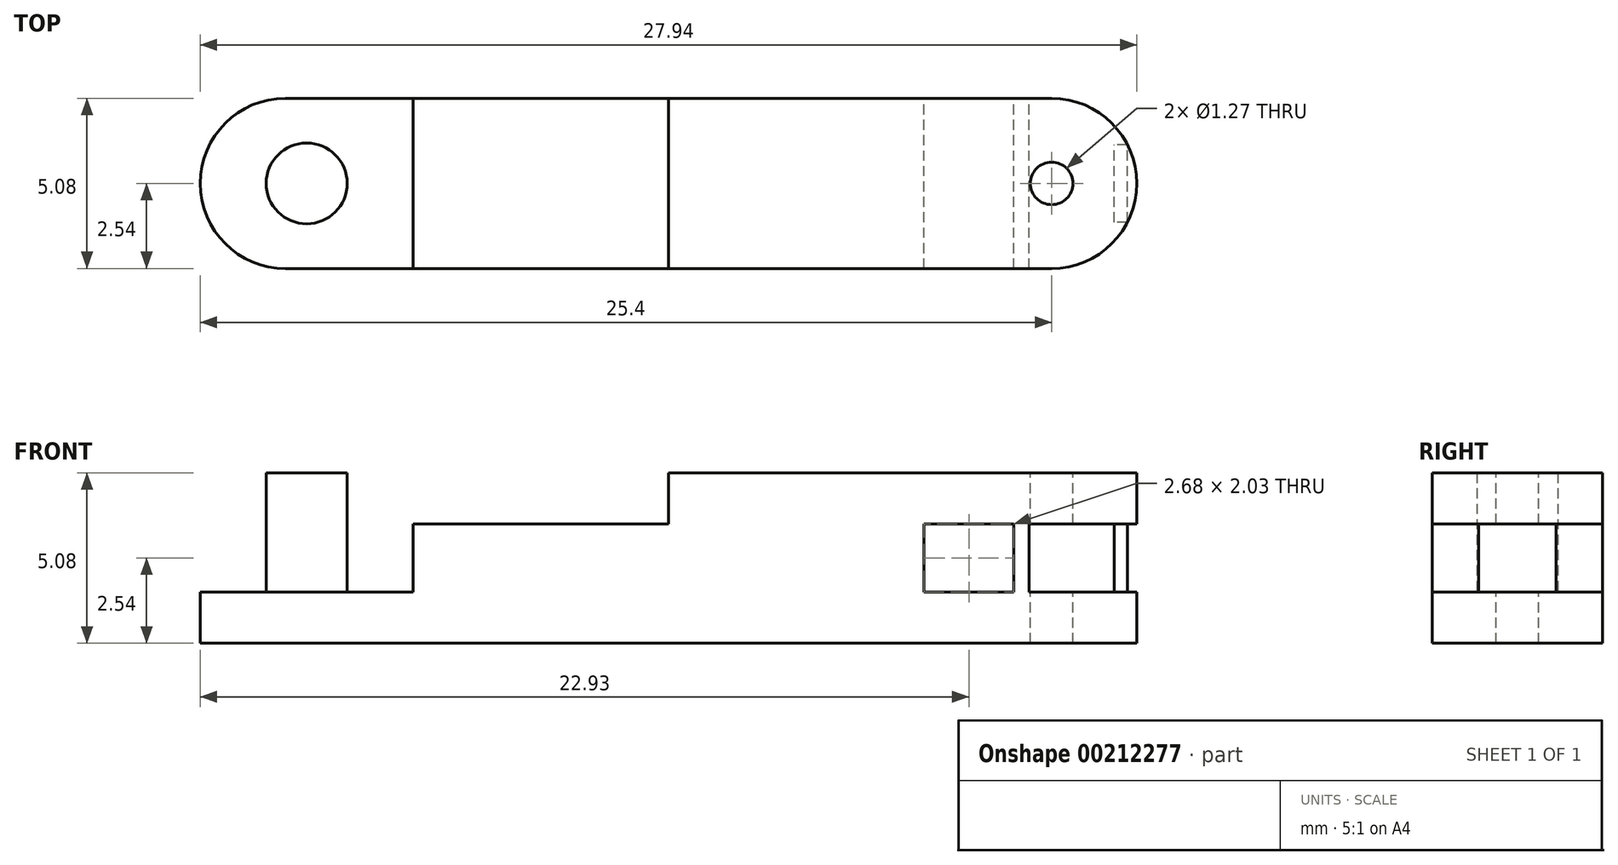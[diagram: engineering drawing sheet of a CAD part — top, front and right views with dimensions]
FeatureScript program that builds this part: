
annotation { "Feature Type Name" : "Feature", "Feature Type Description" : "" }
export const myFeature = defineFeature(function(context is Context, id is Id, definition is map)
    precondition{}
    {
        {
            var Q0;
            Q0=qCreatedBy(makeId("Top.planeOp"),FACE);
            var sketch = newSketch(context, id + "F0", { "sketchPlane" : qUnion([Q0])});
            skLineSegment(sketch, "E0.bottom", {"start": v(13.97, -2.54) * mm, "end": v(-13.97, -2.54) * mm});
            skLineSegment(sketch, "E0.top", {"start": v(13.97, 2.54) * mm, "end": v(-13.97, 2.54) * mm});
            skLineSegment(sketch, "E0.left", {"start": v(13.97, -2.54) * mm, "end": v(13.97, 2.54) * mm});
            skLineSegment(sketch, "E0.right", {"start": v(-13.97, -2.54) * mm, "end": v(-13.97, 2.54) * mm});
            skPoint(sketch, "E0.middle", {"position": v(0, 0) * mm});
            skSolve(sketch);
        }
        {
            var Q0;
            Q0=makeQuery(id+"F0.imprint","IMPRINT",FACE,{"disambiguationData":[TD([[makeQuery(id+"F0.imprint","IMPRINT",EDGE,{"derivedFrom":sQuery(id+"F0.wireOp",EDGE,"E0.bottom")}),-1.0]])]});
            extrude(context, id + "F1", {"entities" : qUnion([Q0]), "depth" : 1.52 * mm});
        }
        {
            var Q0;
            Q0=makeQuery(id+"F1.opExtrude","CAP_FACE",FACE,{"disambiguationData":[OSD([sQuery(id+"F0.wireOp",EDGE,"E0.bottom"),sQuery(id+"F0.wireOp",EDGE,"E0.top"),sQuery(id+"F0.wireOp",EDGE,"E0.left"),sQuery(id+"F0.wireOp",EDGE,"E0.right")])],"isStart":false});
            var sketch = newSketch(context, id + "F2", { "sketchPlane" : qUnion([Q0])});
            skLineSegment(sketch, "E1.bottom", {"start": v(7.62, -2.54) * mm, "end": v(-7.62, -2.54) * mm});
            skLineSegment(sketch, "E1.top", {"start": v(7.62, 2.54) * mm, "end": v(-7.62, 2.54) * mm});
            skLineSegment(sketch, "E1.left", {"start": v(7.62, -2.54) * mm, "end": v(7.62, 2.54) * mm});
            skLineSegment(sketch, "E1.right", {"start": v(-7.62, -2.54) * mm, "end": v(-7.62, 2.54) * mm});
            skPoint(sketch, "E1.middle", {"position": v(0, 0) * mm});
            skSolve(sketch);
        }
        {
            var Q0;
            Q0=makeQuery(id+"F2.imprint","IMPRINT",FACE,{"disambiguationData":[TD([[makeQuery(id+"F2.imprint","IMPRINT",EDGE,{"derivedFrom":sQuery(id+"F2.wireOp",EDGE,"E1.bottom")}),-1.0]])]});
            extrude(context, id + "F3", {"entities" : qUnion([Q0]), "operationType" : NewBodyOperationType.ADD, "depth" : 2.03 * mm});
        }
        {
            var Q0;
            {var subQ0=sQuery(id+"F0.wireOp",EDGE,"E0.right");var subQ1=sQuery(id+"F0.wireOp",EDGE,"E0.top");var subQ2=sQuery(id+"F0.wireOp",EDGE,"E0.bottom");Q0=makeQuery(id+"F3.boolean.opBoolean","SPLIT",FACE,{"disambiguationData":[TD([makeQuery(id+"F1.opExtrude","SWEPT_FACE",FACE,{"disambiguationData":[OSD([subQ0])]})])],"derivedFrom":makeQuery(id+"F1.opExtrude","CAP_FACE",FACE,{"disambiguationData":[OSD([subQ2,subQ1,sQuery(id+"F0.wireOp",EDGE,"E0.left"),subQ0])],"isStart":false})});}
            var sketch = newSketch(context, id + "F4", { "sketchPlane" : qUnion([Q0])});
            skCircle(sketch, "E2", {"center": v(-10.8, 0) * mm, "radius": 1.2 * mm});
            skSolve(sketch);
        }
        {
            var Q0;
            Q0=makeQuery(id+"F4.imprint","IMPRINT",FACE,{"disambiguationData":[TD([[makeQuery(id+"F4.imprint","IMPRINT",EDGE,{"derivedFrom":sQuery(id+"F4.wireOp",EDGE,"E2")}),1.0]])]});
            var Q1;
            Q1=sQuery(id+"F4.wireOp",EDGE,"E2");
            extrude(context, id + "F5", {"entities" : qUnion([Q0]), "operationType" : NewBodyOperationType.ADD, "surfaceEntities" : qUnion([Q1]), "depth" : 3.56 * mm});
        }
        {
            var Q0;
            Q0=makeQuery(id+"F3.opExtrude","CAP_FACE",FACE,{"disambiguationData":[OSD([sQuery(id+"F2.wireOp",EDGE,"E1.bottom"),sQuery(id+"F2.wireOp",EDGE,"E1.top"),sQuery(id+"F2.wireOp",EDGE,"E1.left"),sQuery(id+"F2.wireOp",EDGE,"E1.right")])],"isStart":false});
            var sketch = newSketch(context, id + "F6", { "sketchPlane" : qUnion([Q0])});
            skLineSegment(sketch, "E3.bottom", {"start": v(0, -2.54) * mm, "end": v(13.97, -2.54) * mm});
            skLineSegment(sketch, "E3.top", {"start": v(0, 2.54) * mm, "end": v(13.97, 2.54) * mm});
            skLineSegment(sketch, "E3.left", {"start": v(0, -2.54) * mm, "end": v(0, 2.54) * mm});
            skLineSegment(sketch, "E3.right", {"start": v(13.97, -2.54) * mm, "end": v(13.97, 2.54) * mm});
            skSolve(sketch);
        }
        {
            var Q0;
            Q0 = qSketchRegion(id + "F6", true);
            extrude(context, id + "F7", {"entities" : qUnion([Q0]), "operationType" : NewBodyOperationType.ADD, "depth" : 1.52 * mm});
        }
        {
            var Q0;
            Q0=makeQuery(id+"F7.opExtrude","CAP_FACE",FACE,{"disambiguationData":[OSD([sQuery(id+"F6.wireOp",EDGE,"E3.bottom"),sQuery(id+"F6.wireOp",EDGE,"E3.top"),sQuery(id+"F6.wireOp",EDGE,"E3.left"),sQuery(id+"F6.wireOp",EDGE,"E3.right")])],"isStart":false});
            var sketch = newSketch(context, id + "F8", { "sketchPlane" : qUnion([Q0])});
            skCircle(sketch, "E4", {"center": v(11.43, 0) * mm, "radius": 0.64 * mm});
            skSolve(sketch);
        }
        {
            var Q0;
            Q0 = qSketchRegion(id + "F8", true);
            extrude(context, id + "F9", {"entities" : qUnion([Q0]), "operationType" : NewBodyOperationType.REMOVE, "oppositeDirection" : true, "depth" : 25.4 * mm});
        }
        {
            var Q0;
            Q0=makeQuery(id+"F1.opExtrude","SWEPT_EDGE",EDGE,{"disambiguationData":[OSD([sQuery(id+"F0.wireOp",EDGE,"E0.bottom"),sQuery(id+"F0.wireOp",EDGE,"E0.right")])]});
            var Q1;
            Q1=makeQuery(id+"F1.opExtrude","SWEPT_EDGE",EDGE,{"disambiguationData":[OSD([sQuery(id+"F0.wireOp",EDGE,"E0.top"),sQuery(id+"F0.wireOp",EDGE,"E0.right")])]});
            var Q2;
            Q2=makeQuery(id+"F7.opExtrude","SWEPT_EDGE",EDGE,{"disambiguationData":[OSD([sQuery(id+"F6.wireOp",EDGE,"E3.bottom"),sQuery(id+"F6.wireOp",EDGE,"E3.right")])]});
            var Q3;
            Q3=makeQuery(id+"F1.opExtrude","SWEPT_EDGE",EDGE,{"disambiguationData":[OSD([sQuery(id+"F0.wireOp",EDGE,"E0.bottom"),sQuery(id+"F0.wireOp",EDGE,"E0.left")])]});
            var Q4;
            Q4=makeQuery(id+"F1.opExtrude","SWEPT_EDGE",EDGE,{"disambiguationData":[OSD([sQuery(id+"F0.wireOp",EDGE,"E0.top"),sQuery(id+"F0.wireOp",EDGE,"E0.left")])]});
            var Q5;
            Q5=makeQuery(id+"F7.opExtrude","SWEPT_EDGE",EDGE,{"disambiguationData":[OSD([sQuery(id+"F6.wireOp",EDGE,"E3.top"),sQuery(id+"F6.wireOp",EDGE,"E3.right")])]});
            fillet(context, id + "F10", {"entities" : qUnion([Q0, Q1, Q2, Q3, Q4, Q5]), "radius" : 2.54 * mm, "tangentPropagation" : true, "allowEdgeOverflow" : false});
        }
        {
            var Q0;
            {var subQ0=sQuery(id+"F0.wireOp",EDGE,"E0.left");var subQ1=sQuery(id+"F0.wireOp",EDGE,"E0.top");var subQ2=sQuery(id+"F0.wireOp",EDGE,"E0.bottom");Q0=makeQuery(id+"F3.boolean.opBoolean","SPLIT",FACE,{"disambiguationData":[TD([makeQuery(id+"F1.opExtrude","SWEPT_FACE",FACE,{"disambiguationData":[OSD([subQ0])]})])],"derivedFrom":makeQuery(id+"F1.opExtrude","CAP_FACE",FACE,{"disambiguationData":[OSD([subQ2,subQ1,subQ0,sQuery(id+"F0.wireOp",EDGE,"E0.right")])],"isStart":false})});}
            var sketch = newSketch(context, id + "F11", { "sketchPlane" : qUnion([Q0])});
            skLineSegment(sketch, "E5.bottom", {"start": v(11.43, -2.54) * mm, "end": v(10.75, -2.54) * mm});
            skLineSegment(sketch, "E5.top", {"start": v(10.75, 2.54) * mm, "end": v(10.3, 2.54) * mm});
            skLineSegment(sketch, "E5.left", {"start": v(10.3, -2.54) * mm, "end": v(10.3, 2.54) * mm});
            skLineSegment(sketch, "E5.right", {"start": v(10.75, -2.54) * mm, "end": v(10.75, 2.54) * mm});
            skSolve(sketch);
        }
        {
            var Q0;
            Q0=makeQuery(id+"F11.imprint","IMPRINT",FACE,{"disambiguationData":[TD([[makeQuery(id+"F11.imprint","IMPRINT",EDGE,{"derivedFrom":sQuery(id+"F11.wireOp",EDGE,"E5.top")}),1.0]])]});
            extrude(context, id + "F12", {"entities" : qUnion([Q0]), "operationType" : NewBodyOperationType.ADD, "depth" : 2.03 * mm});
        }
        {
            var Q0;
            {var subQ0=sQuery(id+"F0.wireOp",EDGE,"E0.left");var subQ1=sQuery(id+"F0.wireOp",EDGE,"E0.bottom");var subQ2=sQuery(id+"F0.wireOp",EDGE,"E0.right");var subQ3=sQuery(id+"F0.wireOp",EDGE,"E0.top");var subQ4=makeQuery(id+"F1.opExtrude","CAP_FACE",FACE,{"disambiguationData":[OSD([subQ1,subQ3,subQ0,subQ2])],"isStart":false});Q0=makeQuery(id+"F12.boolean.opBoolean","SPLIT",FACE,{"disambiguationData":[TD([makeQuery(id+"F12.opExtrude","SWEPT_FACE",FACE,{"disambiguationData":[OSD([sQuery(id+"F11.wireOp",EDGE,"E5.right")])]})])],"derivedFrom":makeQuery(id+"F3.boolean.opBoolean","SPLIT",FACE,{"disambiguationData":[TD([makeQuery(id+"F1.opExtrude","SWEPT_FACE",FACE,{"disambiguationData":[OSD([subQ0])]})])],"derivedFrom":subQ4})});}
            var sketch = newSketch(context, id + "F13", { "sketchPlane" : qUnion([Q0])});
            skLineSegment(sketch, "E6.bottom", {"start": v(13.7, -1.16) * mm, "end": v(13.3, -1.16) * mm});
            skLineSegment(sketch, "E6.top", {"start": v(13.7, 1.16) * mm, "end": v(13.3, 1.16) * mm});
            skLineSegment(sketch, "E6.left", {"start": v(13.7, -1.16) * mm, "end": v(13.7, 1.16) * mm});
            skLineSegment(sketch, "E6.right", {"start": v(13.3, -1.16) * mm, "end": v(13.3, 1.16) * mm});
            skSolve(sketch);
        }
        {
            var Q0;
            Q0=makeQuery(id+"F13.imprint","IMPRINT",FACE,{"disambiguationData":[TD([[makeQuery(id+"F13.imprint","IMPRINT",EDGE,{"derivedFrom":sQuery(id+"F13.wireOp",EDGE,"E6.bottom")}),-1.0]])]});
            extrude(context, id + "F14", {"entities" : qUnion([Q0]), "operationType" : NewBodyOperationType.ADD, "depth" : 2.03 * mm});
        }
    });
